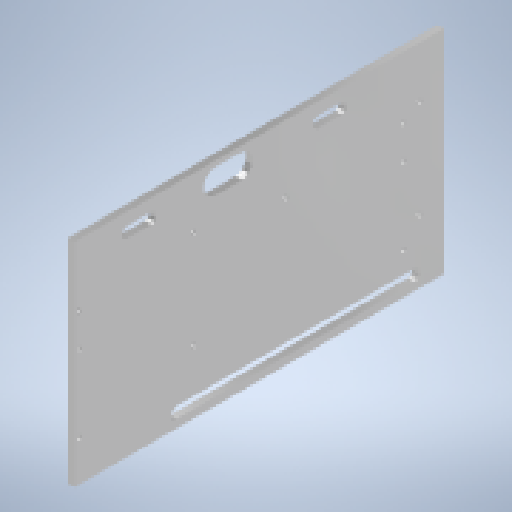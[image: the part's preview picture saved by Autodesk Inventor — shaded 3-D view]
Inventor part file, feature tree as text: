
AUTODESK INVENTOR PART (.ipt)
format: ipt  version: 2024.2 (Build 282272000, 272)  size: 219,136 bytes
history: native  units: mm
features: sketch x5, extrude x4, other x1
ambient origin geometry x8: Origin, YZ Plane, XZ Plane, XY Plane, X Axis, Y Axis, Z Axis, Center Point
bodies: Body1 (feature_tree)
feature tree (10):
  other  "Твердое тело1"
  extrude  "Выдавливание1"  Depth=204.0mm
  extrude  "Выдавливание2"  Depth=130.0mm
  extrude  "Выдавливание3"  Depth=3.0mm
  sketch  "Эскиз4"
  extrude  "Выдавливание4"  Depth=25.0mm
  sketch  "Эскиз1"
  sketch  "Эскиз2"
  sketch  "Эскиз3"
  sketch  "Эскиз5"
